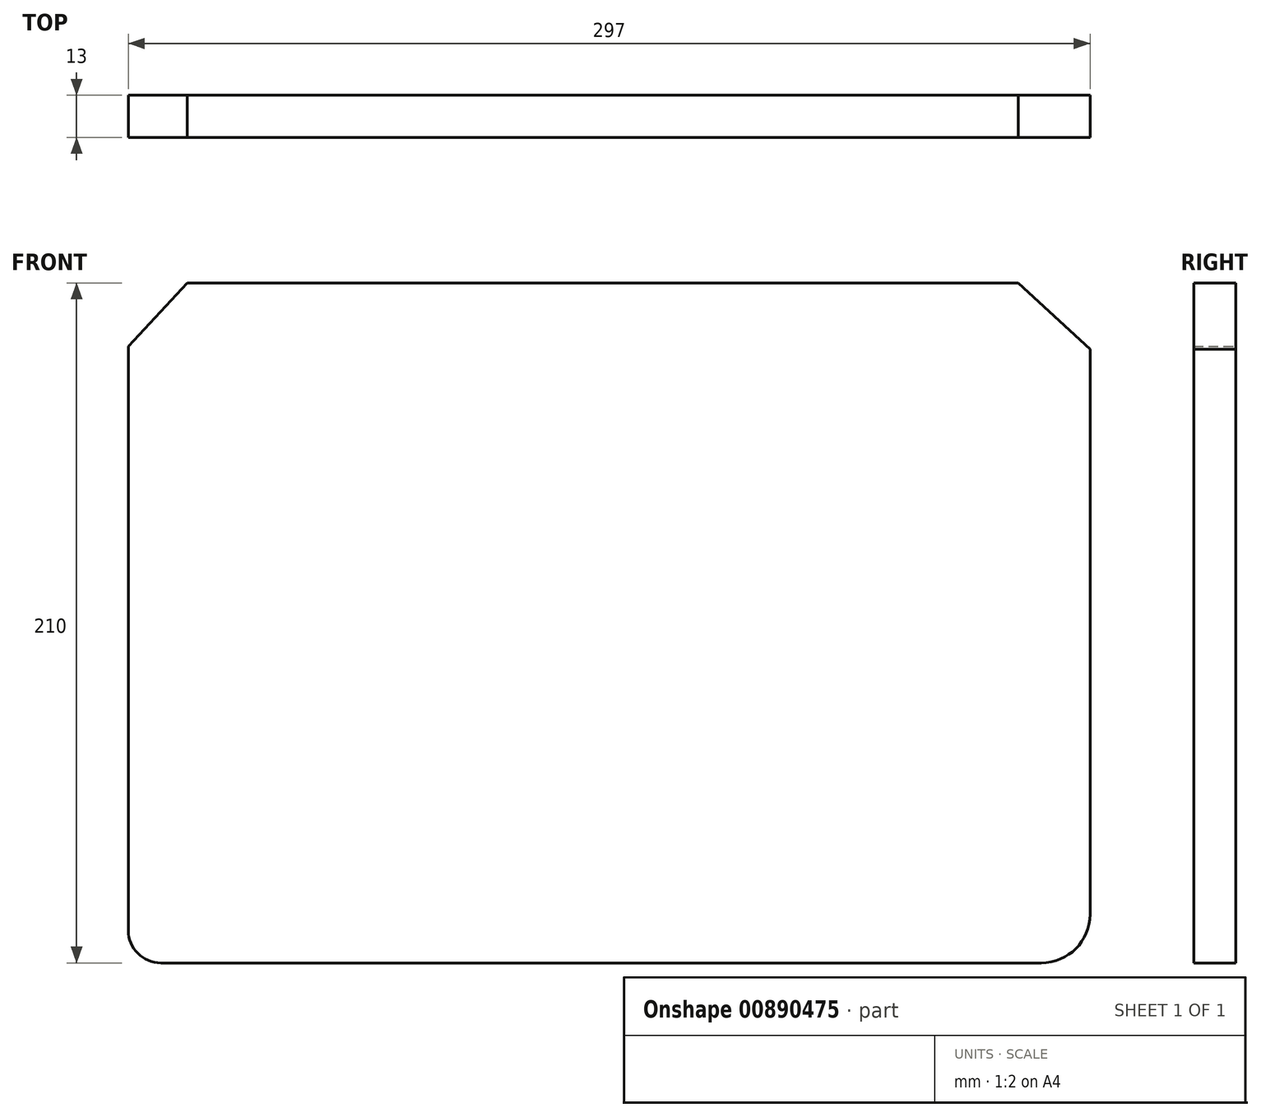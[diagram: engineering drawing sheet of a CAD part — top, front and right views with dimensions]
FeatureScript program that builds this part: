
annotation { "Feature Type Name" : "Feature", "Feature Type Description" : "" }
export const myFeature = defineFeature(function(context is Context, id is Id, definition is map)
    precondition{}
    {
        {
            var Q0;
            Q0=qCreatedBy(makeId("Front.planeOp"),FACE);
            var sketch = newSketch(context, id + "F0", { "sketchPlane" : qUnion([Q0])});
            skLineSegment(sketch, "E0.bottom", {"start": v(-177.07, 62.7) * mm, "end": v(79.65, 62.7) * mm});
            skLineSegment(sketch, "E0.top", {"start": v(-185.2, -147.3) * mm, "end": v(86.8, -147.3) * mm});
            skLineSegment(sketch, "E0.left", {"start": v(-195.2, 43.12) * mm, "end": v(-195.2, -137.3) * mm});
            skLineSegment(sketch, "E0.right", {"start": v(101.8, 42.2) * mm, "end": v(101.8, -132.3) * mm});
            skLineSegment(sketch, "E1", {"start": v(-177.07, 62.7) * mm, "end": v(-195.2, 43.12) * mm});
            skLineSegment(sketch, "E2", {"start": v(79.65, 62.7) * mm, "end": v(101.8, 42.2) * mm});
            skPoint(sketch, "E3.visualSharp", {"position": v(-195.2, -147.3) * mm});
            skArc(sketch, "E3.filletArc", {"start": v(-195.2, -137.3) * mm, "mid": v(-192.26, -144.37) * mm, "end": v(-185.2, -147.3) * mm});
            skPoint(sketch, "E4.visualSharp", {"position": v(101.8, -147.3) * mm});
            skArc(sketch, "E4.filletArc", {"start": v(86.8, -147.3) * mm, "mid": v(97.41, -142.9) * mm, "end": v(101.8, -132.3) * mm});
            skLineSegment(sketch, "E5.bottom", {"start": v(-195.2, -124.7) * mm, "end": v(-75.2, -124.7) * mm});
            skLineSegment(sketch, "E5.top", {"start": v(-195.2, -109.7) * mm, "end": v(-75.2, -109.7) * mm});
            skLineSegment(sketch, "E5.left", {"start": v(-195.2, -124.7) * mm, "end": v(-195.2, -109.7) * mm});
            skLineSegment(sketch, "E5.right", {"start": v(-75.2, -124.7) * mm, "end": v(-75.2, -109.7) * mm});
            skLineSegment(sketch, "E6.bottom", {"start": v(101.8, -125.32) * mm, "end": v(-18.2, -125.32) * mm});
            skLineSegment(sketch, "E6.top", {"start": v(101.8, -82.32) * mm, "end": v(-18.2, -82.32) * mm});
            skLineSegment(sketch, "E6.left", {"start": v(101.8, -125.32) * mm, "end": v(101.8, -82.32) * mm});
            skLineSegment(sketch, "E6.right", {"start": v(-18.2, -125.32) * mm, "end": v(-18.2, -82.32) * mm});
            skLineSegment(sketch, "E7.bottom", {"start": v(-195.2, -82.32) * mm, "end": v(-75.2, -82.32) * mm});
            skLineSegment(sketch, "E7.top", {"start": v(-195.2, -92.32) * mm, "end": v(-75.2, -92.32) * mm});
            skLineSegment(sketch, "E7.left", {"start": v(-195.2, -82.32) * mm, "end": v(-195.2, -92.32) * mm});
            skLineSegment(sketch, "E7.right", {"start": v(-75.2, -82.32) * mm, "end": v(-75.2, -92.32) * mm});
            skSolve(sketch);
        }
        {
            var Q0;
            Q0 = qSketchRegion(id + "F0", true);
            extrude(context, id + "F1", {"entities" : qUnion([Q0]), "depth" : 13 * mm, "offsetDistance" : 25 * mm});
        }
    });
